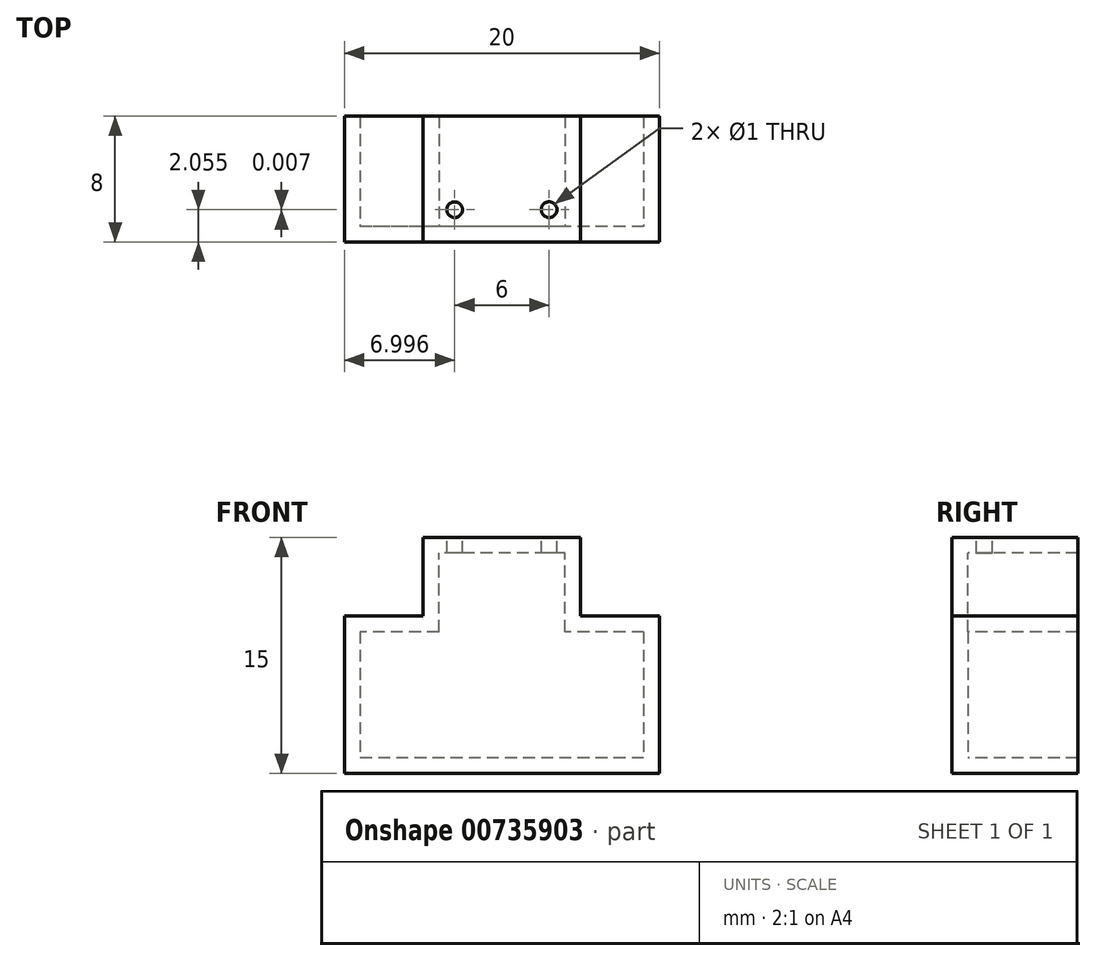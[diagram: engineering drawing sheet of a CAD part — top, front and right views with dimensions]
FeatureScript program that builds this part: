
annotation { "Feature Type Name" : "Feature", "Feature Type Description" : "" }
export const myFeature = defineFeature(function(context is Context, id is Id, definition is map)
    precondition{}
    {
        {
            var Q0;
            Q0=qCreatedBy(makeId("Front.planeOp"),FACE);
            var sketch = newSketch(context, id + "F0", { "sketchPlane" : qUnion([Q0])});
            skLineSegment(sketch, "E0.bottom", {"start": v(59.23, 4.67) * mm, "end": v(39.23, 4.67) * mm});
            skLineSegment(sketch, "E0.top", {"start": v(59.23, 14.67) * mm, "end": v(39.23, 14.67) * mm});
            skLineSegment(sketch, "E0.left", {"start": v(59.23, 4.67) * mm, "end": v(59.23, 14.67) * mm});
            skLineSegment(sketch, "E0.right", {"start": v(39.23, 4.67) * mm, "end": v(39.23, 14.67) * mm});
            skLineSegment(sketch, "E1.bottom", {"start": v(54.23, 14.67) * mm, "end": v(44.23, 14.67) * mm});
            skLineSegment(sketch, "E1.top", {"start": v(54.23, 19.67) * mm, "end": v(44.23, 19.67) * mm});
            skLineSegment(sketch, "E1.left", {"start": v(54.23, 14.67) * mm, "end": v(54.23, 19.67) * mm});
            skLineSegment(sketch, "E1.right", {"start": v(44.23, 14.67) * mm, "end": v(44.23, 19.67) * mm});
            skSolve(sketch);
        }
        {
            var Q0;
            Q0=makeQuery(id+"F0.imprint","IMPRINT",FACE,{"disambiguationData":[TD([[makeQuery(id+"F0.imprint","IMPRINT",EDGE,{"derivedFrom":sQuery(id+"F0.wireOp",EDGE,"E1.top")}),1.0]])]});
            var Q1;
            Q1=makeQuery(id+"F0.imprint","IMPRINT",FACE,{"disambiguationData":[TD([[makeQuery(id+"F0.imprint","IMPRINT",EDGE,{"derivedFrom":sQuery(id+"F0.wireOp",EDGE,"E0.bottom")}),-1.0]])]});
            extrude(context, id + "F1", {"entities" : qUnion([Q0, Q1]), "oppositeDirection" : true, "depth" : 1 * mm, "offsetDistance" : 25 * mm});
        }
        {
            var Q0;
            Q0=makeQuery(id+"F1.opExtrude","CAP_FACE",FACE,{"disambiguationData":[OSD([sQuery(id+"F0.wireOp",EDGE,"E0.bottom"),sQuery(id+"F0.wireOp",EDGE,"E0.top"),sQuery(id+"F0.wireOp",EDGE,"E0.left"),sQuery(id+"F0.wireOp",EDGE,"E0.right"),sQuery(id+"F0.wireOp",EDGE,"E1.top"),sQuery(id+"F0.wireOp",EDGE,"E1.left"),sQuery(id+"F0.wireOp",EDGE,"E1.right")])],"isStart":false});
            var sketch = newSketch(context, id + "F2", { "sketchPlane" : qUnion([Q0])});
            skLineSegment(sketch, "E2.bottom", {"start": v(-58.23, 13.67) * mm, "end": v(-40.23, 13.67) * mm});
            skLineSegment(sketch, "E2.top", {"start": v(-58.23, 5.67) * mm, "end": v(-40.23, 5.67) * mm});
            skLineSegment(sketch, "E2.left", {"start": v(-58.23, 13.67) * mm, "end": v(-58.23, 5.67) * mm});
            skLineSegment(sketch, "E2.right", {"start": v(-40.23, 13.67) * mm, "end": v(-40.23, 5.67) * mm});
            skLineSegment(sketch, "E3.bottom", {"start": v(-53.23, 13.67) * mm, "end": v(-45.23, 13.67) * mm});
            skLineSegment(sketch, "E3.top", {"start": v(-53.23, 18.67) * mm, "end": v(-45.23, 18.67) * mm});
            skLineSegment(sketch, "E3.left", {"start": v(-53.23, 13.67) * mm, "end": v(-53.23, 18.67) * mm});
            skLineSegment(sketch, "E3.right", {"start": v(-45.23, 13.67) * mm, "end": v(-45.23, 18.67) * mm});
            skSolve(sketch);
        }
        {
            var Q0;
            Q0=makeQuery(id+"F2.imprint","IMPRINT",FACE,{"disambiguationData":[TD([[makeQuery(id+"F2.imprint","IMPRINT",EDGE,{"derivedFrom":sQuery(id+"F2.wireOp",EDGE,"E2.top")}),-1.0]])]});
            extrude(context, id + "F3", {"entities" : qUnion([Q0]), "operationType" : NewBodyOperationType.ADD, "depth" : 7 * mm, "offsetDistance" : 25 * mm});
        }
        {
            var Q0;
            {var subQ0=sQuery(id+"F0.wireOp",EDGE,"E1.top");Q0=makeQuery(id+"F3.boolean.opBoolean","MERGE",FACE,{"derivedFrom":[makeQuery(id+"F1.opExtrude","SWEPT_FACE",FACE,{"disambiguationData":[OSD([subQ0])]}),makeQuery(id+"F3.opExtrude","SWEPT_FACE",FACE,{"disambiguationData":[OSD([subQ0])]})]});}
            var sketch = newSketch(context, id + "F4", { "sketchPlane" : qUnion([Q0])});
            skCircle(sketch, "E4", {"center": v(46.23, 2.05) * mm, "radius": 0.5 * mm});
            skCircle(sketch, "E5", {"center": v(52.23, 2.06) * mm, "radius": 0.5 * mm});
            skSolve(sketch);
        }
        {
            var Q0;
            Q0=sQuery(id+"F4.wireOp",VERTEX,"E4.center");
            var Q1;
            Q1=sQuery(id+"F4.wireOp",VERTEX,"E5.center");
            var Q2;
            Q2=makeQuery(id+"F1.opExtrude","SWEPT_BODY",BODY,{"disambiguationData":[OSD([sQuery(id+"F0.wireOp",EDGE,"E0.bottom"),sQuery(id+"F0.wireOp",EDGE,"E0.top"),sQuery(id+"F0.wireOp",EDGE,"E0.left"),sQuery(id+"F0.wireOp",EDGE,"E0.right"),sQuery(id+"F0.wireOp",EDGE,"E1.top"),sQuery(id+"F0.wireOp",EDGE,"E1.left"),sQuery(id+"F0.wireOp",EDGE,"E1.right")])]});
            hole(context, id + "F5", {"style" : HoleStyle.SIMPLE, "endStyle" : HoleEndStyle.BLIND, "holeDiameter" : 1 * mm, "majorDiameter" : 5 * mm, "holeDepth" : 1 * mm, "isTappedThrough" : true, "tappedDepth" : 12 * mm, "tapClearance" : 3, "locations" : qUnion([Q0, Q1]), "scope" : qUnion([Q2])});
        }
    });
